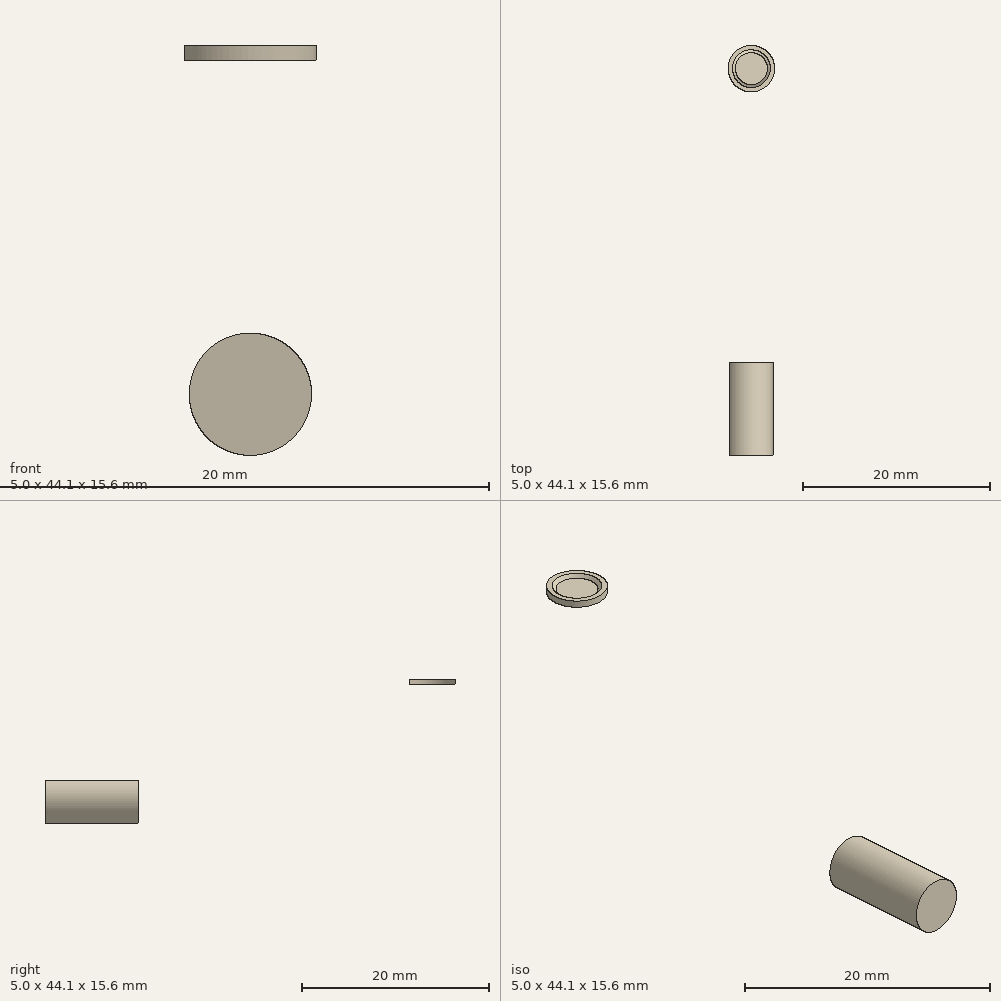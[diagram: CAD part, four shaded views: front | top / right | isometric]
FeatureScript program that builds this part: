
annotation { "Feature Type Name" : "Feature", "Feature Type Description" : "" }
export const myFeature = defineFeature(function(context is Context, id is Id, definition is map)
    precondition{}
    {
        {
            var Q0;
            Q0=qCreatedBy(makeId("Front.planeOp"),FACE);
            var sketch = newSketch(context, id + "F0", { "sketchPlane" : qUnion([Q0])});
            skCircle(sketch, "E0", {"center": v(0, 0) * mm, "radius": 2.33 * mm});
            skSolve(sketch);
        }
        {
            var Q0;
            Q0 = qSketchRegion(id + "F0", true);
            extrude(context, id + "F1", {"entities" : qUnion([Q0]), "depth" : 10 * mm});
        }
        {
            var Q0;
            Q0=qCreatedBy(makeId("Right.planeOp"),FACE);
            var sketch = newSketch(context, id + "F2", { "sketchPlane" : qUnion([Q0])});
            skLineSegment(sketch, "E1", {"start": v(31.58, 12.68) * mm, "end": v(29.08, 12.68) * mm});
            skLineSegment(sketch, "E2", {"start": v(29.08, 12.68) * mm, "end": v(29.08, 13.26) * mm});
            skLineSegment(sketch, "E3", {"start": v(29.08, 13.26) * mm, "end": v(29.55, 13.26) * mm});
            skLineSegment(sketch, "E4", {"start": v(29.55, 13.26) * mm, "end": v(29.86, 12.98) * mm});
            skLineSegment(sketch, "E5", {"start": v(29.86, 12.98) * mm, "end": v(31.58, 12.98) * mm});
            skLineSegment(sketch, "E6", {"start": v(31.58, 12.98) * mm, "end": v(31.58, 12.68) * mm});
            skSolve(sketch);
        }
        {
            var Q0;
            Q0 = qSketchRegion(id + "F2", true);
            var Q1;
            Q1=sQuery(id+"F2.wireOp",EDGE,"E6");
            revolve(context, id + "F3", {"entities" : qUnion([Q0]), "axis" : qUnion([Q1]), "revolveType" : RevolveType.FULL});
        }
    });
